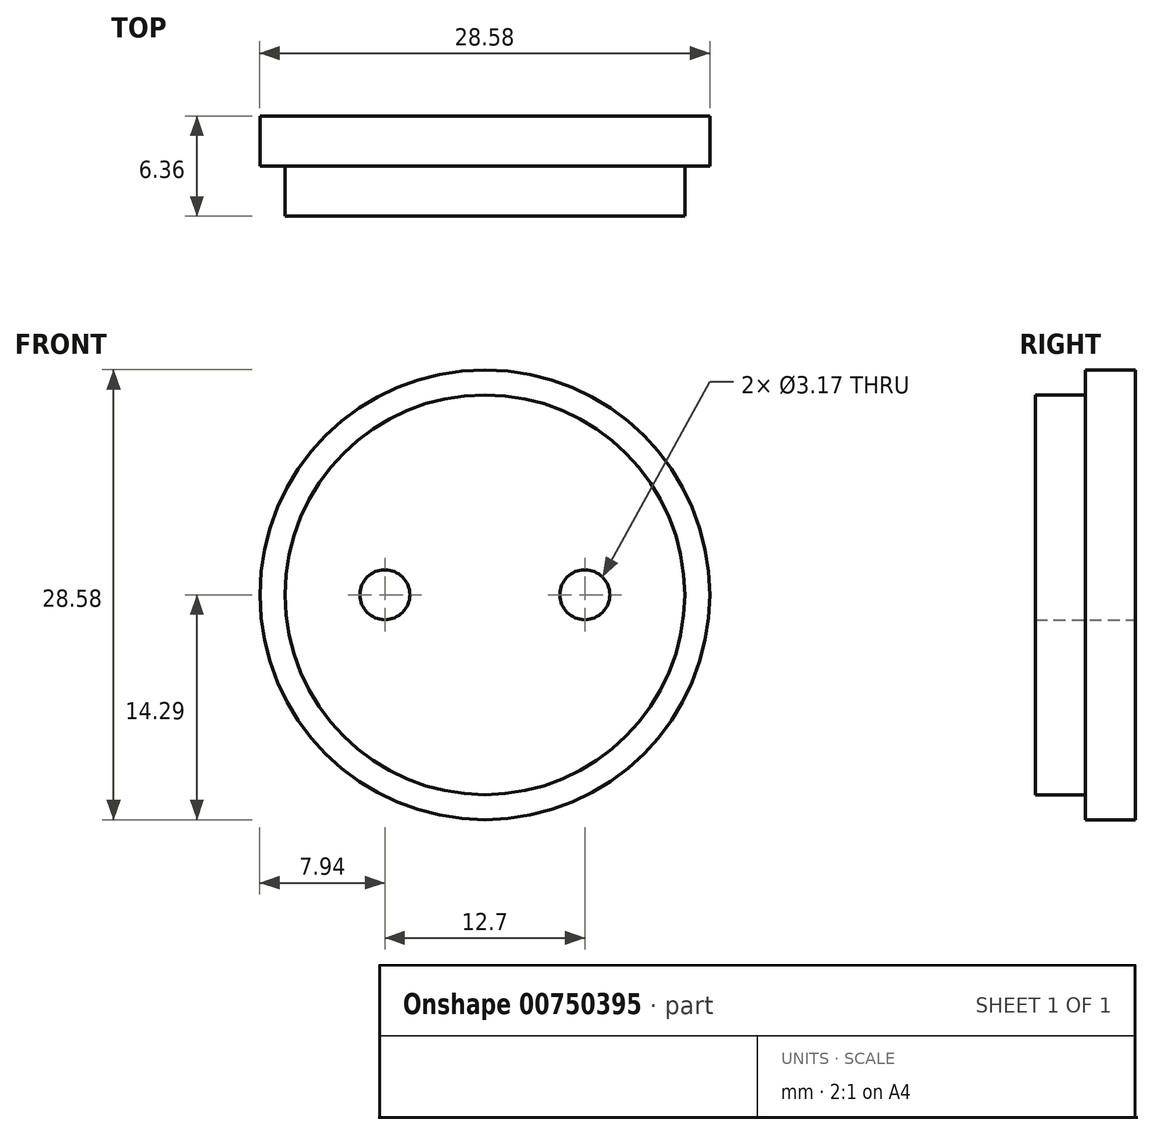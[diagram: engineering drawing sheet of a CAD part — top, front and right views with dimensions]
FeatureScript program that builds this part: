
annotation { "Feature Type Name" : "Feature", "Feature Type Description" : "" }
export const myFeature = defineFeature(function(context is Context, id is Id, definition is map)
    precondition{}
    {
        {
            var Q0;
            Q0=qCreatedBy(makeId("Front.planeOp"),FACE);
            var sketch = newSketch(context, id + "F0", { "sketchPlane" : qUnion([Q0])});
            skCircle(sketch, "E0", {"center": v(0, 0) * mm, "radius": 12.7 * mm});
            skCircle(sketch, "E1", {"center": v(-6.35, 0) * mm, "radius": 1.59 * mm});
            skCircle(sketch, "E2", {"center": v(6.35, 0) * mm, "radius": 1.59 * mm});
            skLineSegment(sketch, "E3", {"start": v(-6.35, 0) * mm, "end": v(6.35, 0) * mm, "construction": true});
            skSolve(sketch);
        }
        {
            var Q0;
            Q0=makeQuery(id+"F0.imprint","IMPRINT",FACE,{"disambiguationData":[TD([[makeQuery(id+"F0.imprint","IMPRINT",EDGE,{"derivedFrom":sQuery(id+"F0.wireOp",EDGE,"E0")}),1.0]])]});
            extrude(context, id + "F1", {"entities" : qUnion([Q0]), "depth" : 3.17 * mm, "offsetDistance" : 25.4 * mm});
        }
        {
            var Q0;
            Q0=makeQuery(id+"F1.opExtrude","CAP_FACE",FACE,{"disambiguationData":[OSD([sQuery(id+"F0.wireOp",EDGE,"E0"),sQuery(id+"F0.wireOp",EDGE,"E1"),sQuery(id+"F0.wireOp",EDGE,"E2")])],"isStart":true});
            var sketch = newSketch(context, id + "F2", { "sketchPlane" : qUnion([Q0])});
            skCircle(sketch, "E4", {"center": v(0, 0) * mm, "radius": 14.29 * mm});
            skCircle(sketch, "E5.0", {"center": v(-6.35, 0) * mm, "radius": 1.59 * mm});
            skCircle(sketch, "E6.0", {"center": v(6.35, 0) * mm, "radius": 1.59 * mm});
            skSolve(sketch);
        }
        {
            var Q0;
            Q0 = qSketchRegion(id + "F2", true);
            extrude(context, id + "F3", {"entities" : qUnion([Q0]), "operationType" : NewBodyOperationType.ADD, "depth" : 3.17 * mm, "offsetDistance" : 25.4 * mm});
        }
    });
